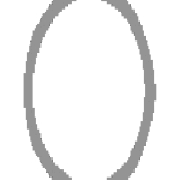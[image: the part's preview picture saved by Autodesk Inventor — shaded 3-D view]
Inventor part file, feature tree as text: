
AUTODESK INVENTOR PART (.ipt)
format: ipt  version: 2021 (Build 250183000, 183)  size: 113,152 bytes
history: native  units: in
note: dims shown in document units (in); Inventor stores cm internally (conversion verified against a paired STEP export)
features: other x4, sketch x3, plane x1
ambient origin geometry x8: Origin, YZ Plane, XZ Plane, XY Plane, X Axis, Y Axis, Z Axis, Center Point
bodies: Solid1 (feature_tree), Body (feature_tree)
feature tree (8):
  other  "Driven Length"
  other  "Frame Generator"
  other  "Start Plane"
  other  "End Plane"
  sketch  "Sketch"  dims[d2=15.5in d4=-0.0in d5=15.5in d6=0.12in d7=0.0in d8=90.0deg d9=15.5in]
  sketch  "Sketch2"  dims[d0=1.0in]
  plane  "Work Plane3"
  sketch  "Sketch3"  dims[d1=0.065in]
